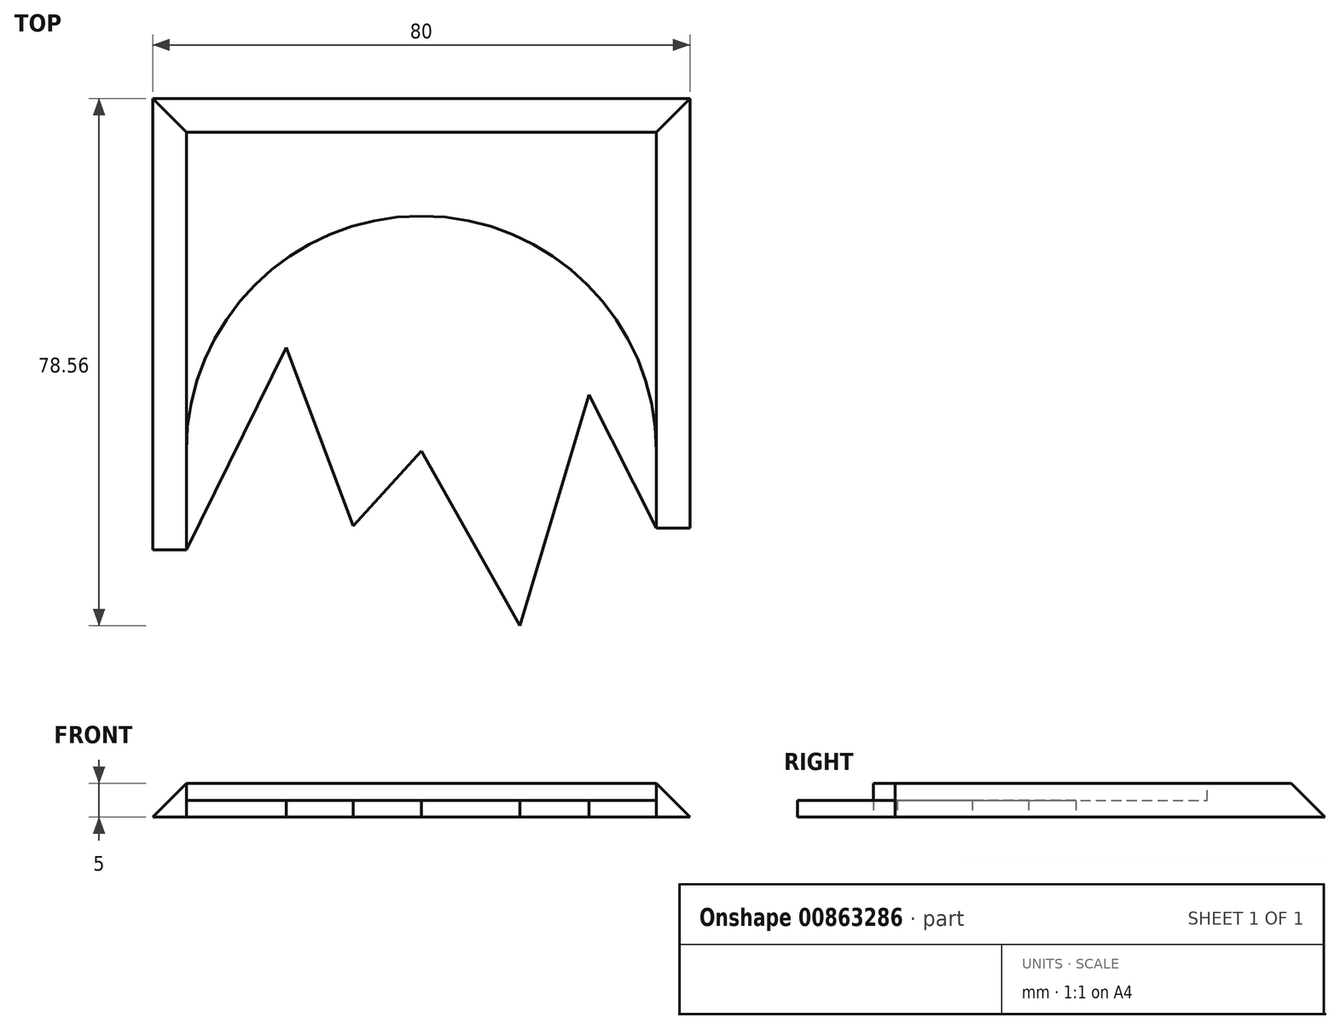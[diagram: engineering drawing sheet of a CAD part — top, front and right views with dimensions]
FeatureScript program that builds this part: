
annotation { "Feature Type Name" : "Feature", "Feature Type Description" : "" }
export const myFeature = defineFeature(function(context is Context, id is Id, definition is map)
    precondition{}
    {
        {
            var Q0;
            Q0=qCreatedBy(makeId("Top.planeOp"),FACE);
            var sketch = newSketch(context, id + "F0", { "sketchPlane" : qUnion([Q0])});
            skLineSegment(sketch, "E0.bottom", {"start": v(35, -47.5) * mm, "end": v(-35, -47.5) * mm});
            skLineSegment(sketch, "E0.top", {"start": v(35, 47.5) * mm, "end": v(-35, 47.5) * mm});
            skLineSegment(sketch, "E0.left", {"start": v(35, -47.5) * mm, "end": v(35, 47.5) * mm});
            skLineSegment(sketch, "E0.right", {"start": v(-35, -47.5) * mm, "end": v(-35, 47.5) * mm});
            skLineSegment(sketch, "E1.bottom", {"start": v(40, -52.5) * mm, "end": v(-40, -52.5) * mm});
            skLineSegment(sketch, "E1.top", {"start": v(40, 52.5) * mm, "end": v(-40, 52.5) * mm});
            skLineSegment(sketch, "E1.left", {"start": v(40, -52.5) * mm, "end": v(40, 52.5) * mm});
            skLineSegment(sketch, "E1.right", {"start": v(-40, -52.5) * mm, "end": v(-40, 52.5) * mm});
            skLineSegment(sketch, "E2", {"start": v(-35, -14.74) * mm, "end": v(-20.1, 15.44) * mm});
            skLineSegment(sketch, "E3", {"start": v(-20.1, 15.44) * mm, "end": v(-10.15, -11.19) * mm});
            skLineSegment(sketch, "E4", {"start": v(-10.15, -11.19) * mm, "end": v(0, 0) * mm});
            skLineSegment(sketch, "E5", {"start": v(0, 0) * mm, "end": v(14.7, -26.06) * mm});
            skLineSegment(sketch, "E6", {"start": v(14.7, -26.06) * mm, "end": v(25, 8.38) * mm});
            skLineSegment(sketch, "E7", {"start": v(25, 8.38) * mm, "end": v(35, -11.5) * mm});
            skLineSegment(sketch, "E8", {"start": v(35, -11.5) * mm, "end": v(40, -11.5) * mm});
            skLineSegment(sketch, "E9", {"start": v(-35, -14.74) * mm, "end": v(-40, -14.74) * mm});
            skSolve(sketch);
        }
        {
            var Q0;
            {var subQ1=sQuery(id+"F0.wireOp",EDGE,"E0.top");Q0=makeQuery(id+"F0.imprint","IMPRINT",FACE,{"disambiguationData":[TD([[makeQuery(id+"F0.imprint","IMPRINT",EDGE,{"derivedFrom":subQ1}),1.0]])]});}
            var Q1;
            {var subQ3=sQuery(id+"F0.wireOp",EDGE,"E0.top");Q1=makeQuery(id+"F0.imprint","IMPRINT",FACE,{"disambiguationData":[TD([[makeQuery(id+"F0.imprint","IMPRINT",EDGE,{"derivedFrom":subQ3}),-1.0]])]});}
            extrude(context, id + "F1", {"entities" : qUnion([Q0, Q1]), "depth" : 5 * mm, "offsetDistance" : 25 * mm});
        }
        {
            var Q0;
            Q0=makeQuery(id+"F1.opExtrude","CAP_EDGE",EDGE,{"disambiguationData":[OSD([sQuery(id+"F0.wireOp",EDGE,"E1.right")])],"isStart":false});
            var Q1;
            Q1=makeQuery(id+"F1.opExtrude","CAP_EDGE",EDGE,{"disambiguationData":[OSD([sQuery(id+"F0.wireOp",EDGE,"E1.bottom")])],"isStart":false});
            var Q2;
            Q2=makeQuery(id+"F1.opExtrude","CAP_EDGE",EDGE,{"disambiguationData":[OSD([sQuery(id+"F0.wireOp",EDGE,"E1.left")])],"isStart":false});
            var Q3;
            Q3=makeQuery(id+"F1.opExtrude","CAP_EDGE",EDGE,{"disambiguationData":[OSD([sQuery(id+"F0.wireOp",EDGE,"E1.top")])],"isStart":false});
            chamfer(context, id + "F2", {"entities" : qUnion([Q0, Q1, Q2, Q3]), "width" : 5 * mm, "tangentPropagation" : true});
        }
        {
            var Q0;
            Q0=makeQuery(id+"F1.opExtrude","CAP_FACE",FACE,{"disambiguationData":[OSD([sQuery(id+"F0.wireOp",EDGE,"E1.top"),sQuery(id+"F0.wireOp",EDGE,"E1.left"),sQuery(id+"F0.wireOp",EDGE,"E1.right"),sQuery(id+"F0.wireOp",EDGE,"E2"),sQuery(id+"F0.wireOp",EDGE,"E3"),sQuery(id+"F0.wireOp",EDGE,"E4"),sQuery(id+"F0.wireOp",EDGE,"E5"),sQuery(id+"F0.wireOp",EDGE,"E6"),sQuery(id+"F0.wireOp",EDGE,"E7"),sQuery(id+"F0.wireOp",EDGE,"E8"),sQuery(id+"F0.wireOp",EDGE,"E9")])],"isStart":false});
            var sketch = newSketch(context, id + "F3", { "sketchPlane" : qUnion([Q0])});
            skCircle(sketch, "E10", {"center": v(0, 0) * mm, "radius": 35 * mm});
            skLineSegment(sketch, "E11", {"start": v(-35, 0) * mm, "end": v(-35, -22.53) * mm});
            skLineSegment(sketch, "E12", {"start": v(-35, -22.53) * mm, "end": v(35, -22.53) * mm});
            skLineSegment(sketch, "E13", {"start": v(35, -22.53) * mm, "end": v(35, 0) * mm});
            skSolve(sketch);
        }
        {
            var Q0;
            {var subQ0=sQuery(id+"F3.wireOp",EDGE,"E13");var subQ2=sQuery(id+"F0.wireOp",EDGE,"E7");var subQ5=makeQuery(id+"F1.opExtrude","CAP_EDGE",EDGE,{"disambiguationData":[OSD([subQ2])],"isStart":false});var subQ7=makeQuery(id+"F3.imprint","INTERSECT",VERTEX,{"derivedFrom":[subQ5,subQ0]});Q0=makeQuery(id+"F3.imprint","IMPRINT",FACE,{"disambiguationData":[TD([[makeQuery(id+"F3.imprint","IMPRINT",EDGE,{"disambiguationData":[TD([[subQ7,1.0]])],"derivedFrom":subQ5}),1.0]])]});}
            var Q1;
            {var subQ5=sQuery(id+"F0.wireOp",EDGE,"E3");var subQ22=makeQuery(id+"F1.opExtrude","CAP_EDGE",EDGE,{"disambiguationData":[OSD([subQ5])],"isStart":false});Q1=makeQuery(id+"F3.imprint","IMPRINT",FACE,{"disambiguationData":[TD([[makeQuery(id+"F3.imprint","IMPRINT",EDGE,{"derivedFrom":subQ22}),1.0]])]});}
            var Q2;
            {var subQ0=sQuery(id+"F3.wireOp",EDGE,"E11");var subQ2=sQuery(id+"F0.wireOp",EDGE,"E2");var subQ5=makeQuery(id+"F1.opExtrude","CAP_EDGE",EDGE,{"disambiguationData":[OSD([subQ2])],"isStart":false});var subQ7=makeQuery(id+"F3.imprint","INTERSECT",VERTEX,{"derivedFrom":[subQ5,subQ0]});Q2=makeQuery(id+"F3.imprint","IMPRINT",FACE,{"disambiguationData":[TD([[makeQuery(id+"F3.imprint","IMPRINT",EDGE,{"disambiguationData":[TD([[subQ7,-1.0]])],"derivedFrom":subQ5}),1.0]])]});}
            var Q3;
            {var subQ0=sQuery(id+"F3.wireOp",EDGE,"E12");var subQ1=makeQuery(id+"F1.opExtrude","CAP_EDGE",EDGE,{"disambiguationData":[OSD([sQuery(id+"F0.wireOp",EDGE,"E5")])],"isStart":false});var subQ2=makeQuery(id+"F3.imprint","INTERSECT",VERTEX,{"derivedFrom":[subQ1,subQ0]});Q3=makeQuery(id+"F3.imprint","IMPRINT",FACE,{"disambiguationData":[TD([[makeQuery(id+"F3.imprint","IMPRINT",EDGE,{"disambiguationData":[TD([[subQ2,-1.0]])],"derivedFrom":subQ0}),-1.0]])]});}
            extrude(context, id + "F4", {"entities" : qUnion([Q0, Q1, Q2, Q3]), "operationType" : NewBodyOperationType.REMOVE, "oppositeDirection" : true, "depth" : 2.5 * mm, "offsetDistance" : 25 * mm});
        }
    });
